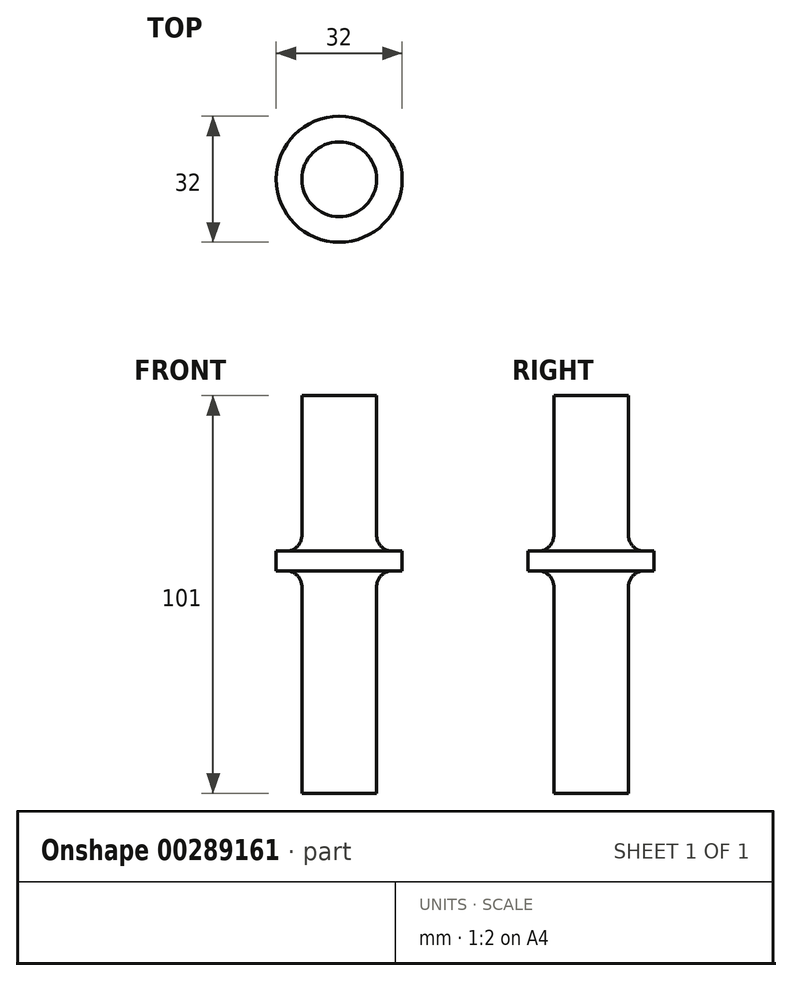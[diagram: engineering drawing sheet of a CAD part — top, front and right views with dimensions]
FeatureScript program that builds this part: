
annotation { "Feature Type Name" : "Feature", "Feature Type Description" : "" }
export const myFeature = defineFeature(function(context is Context, id is Id, definition is map)
    precondition{}
    {
        {
            var Q0;
            Q0=qCreatedBy(makeId("Top.planeOp"),FACE);
            var sketch = newSketch(context, id + "F0", { "sketchPlane" : qUnion([Q0])});
            skCircle(sketch, "E0", {"center": v(0, 0) * mm, "radius": 9.5 * mm});
            skSolve(sketch);
        }
        {
            var Q0;
            Q0=makeQuery(id+"F0.imprint","IMPRINT",FACE,{"disambiguationData":[TD([[makeQuery(id+"F0.imprint","IMPRINT",EDGE,{"derivedFrom":sQuery(id+"F0.wireOp",EDGE,"E0")}),1.0]])]});
            extrude(context, id + "F1", {"entities" : qUnion([Q0]), "depth" : 42 * mm, "hasSecondDirection" : true, "secondDirectionOppositeDirection" : true, "secondDirectionDepth" : 59 * mm});
        }
        {
            var Q0;
            Q0=qCreatedBy(makeId("Top.planeOp"),FACE);
            var sketch = newSketch(context, id + "F2", { "sketchPlane" : qUnion([Q0])});
            skCircle(sketch, "E1", {"center": v(0, 0) * mm, "radius": 16 * mm});
            skSolve(sketch);
        }
        {
            var Q0;
            Q0=makeQuery(id+"F2.imprint","IMPRINT",FACE,{"disambiguationData":[TD([[makeQuery(id+"F2.imprint","IMPRINT",EDGE,{"derivedFrom":sQuery(id+"F2.wireOp",EDGE,"E1")}),1.0]])]});
            extrude(context, id + "F3", {"entities" : qUnion([Q0]), "operationType" : NewBodyOperationType.ADD, "depth" : 2.5 * mm, "hasSecondDirection" : true, "secondDirectionOppositeDirection" : true, "secondDirectionDepth" : 2.5 * mm});
        }
        {
            var Q0;
            Q0=makeQuery(id+"F3.boolean.opBoolean","INTERSECT",EDGE,{"derivedFrom":[makeQuery(id+"F1.opExtrude","SWEPT_FACE",FACE,{"disambiguationData":[OSD([sQuery(id+"F0.wireOp",EDGE,"E0")])]}),makeQuery(id+"F3.opExtrude","CAP_FACE",FACE,{"disambiguationData":[OSD([sQuery(id+"F2.wireOp",EDGE,"E1")])],"isStart":false})]});
            var Q1;
            Q1=makeQuery(id+"F3.boolean.opBoolean","INTERSECT",EDGE,{"derivedFrom":[makeQuery(id+"F1.opExtrude","SWEPT_FACE",FACE,{"disambiguationData":[OSD([sQuery(id+"F0.wireOp",EDGE,"E0")])]}),makeQuery(id+"F3.opExtrude","CAP_FACE",FACE,{"disambiguationData":[OSD([sQuery(id+"F2.wireOp",EDGE,"E1")])],"isStart":true})]});
            fillet(context, id + "F4", {"entities" : qUnion([Q0, Q1]), "radius" : 4 * mm, "tangentPropagation" : true, "allowEdgeOverflow" : false});
        }
    });
